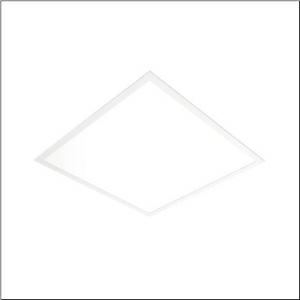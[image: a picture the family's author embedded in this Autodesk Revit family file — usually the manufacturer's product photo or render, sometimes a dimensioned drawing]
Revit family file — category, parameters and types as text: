
# Revit family: apollon_r__41_51mh12wd2443_fb74
name_source: partatom
category: Lighting Fixtures
units: mm (PartAtom-declared; Revit-internal decimal feet)

## family parameters
Cut with Voids When Loaded = No
Host = Face
Light Source = No
Part Type = Normal
Room Calculation Point = No
Round Connector Dimension = Use Diameter
Shared = No

## types (1)
- Apollon® 41 (1 x LED, 3500 lm, 28.5 W, 4000K)
    Apparent Load = 29 VA
    CIE Flux Codes = 61 87 97 100 100
    Color Rendering = 80
    Color Temperature = 4000K
    Default Elevation = 1800 mm
    Description = Apollon® 41, office luminaire, primary optical cover: prismatic diffuser, of PS, light emission: direct distribution, primary light characteristic: symmetric, installation type: lay-in mounting, LED, rated luminous flux: 3.500lm, luminous efficacy: 123lm/W, light colour: 840, colour temperature: 4000K, control gear: DALI 2, with terminal, 5-pole, mains connection: 220..240V, AC, 50/60Hz, housing, of aluminium section, traffic white (RAL 9016), module: M600, length: 595mm, width: 595mm, height: 60mm, recess depth: 180mm, housing upper side, of sheet steel, protection rating (complete): IP20, protection rating (lamp compartment, on room side): IP40, insulation class (complete): insulation class II (safety insulation), certification: CE, ENEC, impact resistance: IK03, permissible operating ambient temperature: -25..+40°C, packaging unit: 1 piece
    Height = 0 mm  [stored 0 ft]
    Lamp = 1 x LED
    Lamp Light Flux = 3500 lm
    Lamp Power = 28.5 W
    Lamp count = 1
    Length = 600 mm
    Luminous efficacy = 123 lm/W
    Manufacturer = Siteco
    ModVariant = No
    Model = 51MH12WD2443
    Mounting Place = Ceiling
    Mounting Type = Recessed
    Number of Poles = 1
    OnlyDefault = Yes
    Power Factor = 1
    Product Name = Apollon® 41
    Product group = office luminaire | ceiling recessed
    ProductGroupID = 401
    Protection Class = Protection class II
    Protection Degree = IP 20
    RLX_Detail_Level = 1
    RLX_Emergency_Light_Flux = 0 lm
    RLX_Emergency_Type = 0
    RLX_Emergency_Type_DB = No
    RlxData = <blob elided: 12269 chars, md5=be8b9681>
    Socket = socket
    Standby Power = 0 W
    System Light Flux = 3500 lm
    System Power = 29 W
    Type Comments = Product without accessories
    Type Image = l_1291024.jpg
    URL = http://relux.com
    VarID = ---
    Voltage = 0 V
    Weight = 0.00 kg
    Width = 600 mm

note: [stored X ft] marks values corroborated as IEEE doubles in the binary element streams (Revit-internal decimal feet)

## geometry (parser evidence)
native form markers: Sweep x11
no freeform markers — native parametric forms only
